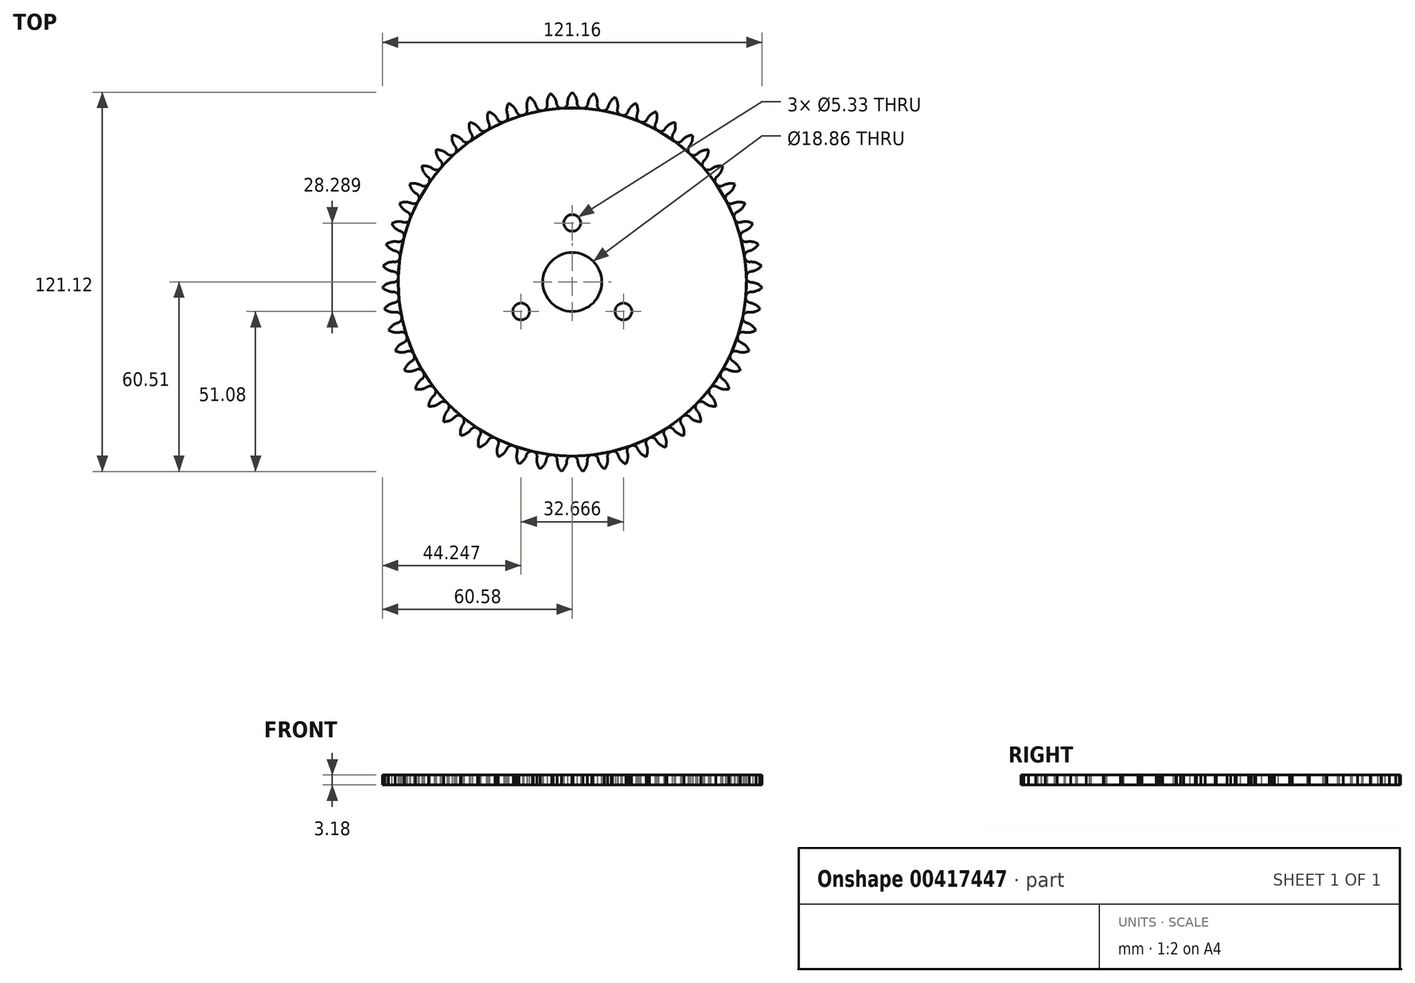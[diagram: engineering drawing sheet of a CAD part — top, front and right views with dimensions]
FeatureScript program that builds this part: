
annotation { "Feature Type Name" : "Feature", "Feature Type Description" : "" }
export const myFeature = defineFeature(function(context is Context, id is Id, definition is map)
    precondition{}
    {
        {
            assignVariable(context, id + "F0", {"name" : "Teeth", "anyValue" : 55});
        }
        {
            var Q0;
            Q0=qCreatedBy(makeId("Top.planeOp"),FACE);
            var sketch = newSketch(context, id + "F1", { "sketchPlane" : qUnion([Q0])});
            skCircle(sketch, "E0", {"center": v(0, 0) * mm, "radius": 55.58 * mm});
            skArc(sketch, "E1", {"start": v(-3.17, 55.5) * mm, "mid": v(-2, 55.98) * mm, "end": v(-1.52, 57.15) * mm});
            skLineSegment(sketch, "E2", {"start": v(-3.18, 57.15) * mm, "end": v(3.18, 57.15) * mm, "construction": true});
            skPoint(sketch, "E3", {"position": v(3.18, 55.5) * mm});
            skPoint(sketch, "E4", {"position": v(3.18, 58.8) * mm});
            skPoint(sketch, "E5", {"position": v(-3.17, 55.5) * mm});
            skPoint(sketch, "E6", {"position": v(-3.17, 58.8) * mm});
            skLineSegment(sketch, "E7", {"start": v(-3.17, 55.5) * mm, "end": v(3.18, 55.5) * mm});
            skLineSegment(sketch, "E8", {"start": v(0, 0) * mm, "end": v(0, 76.2) * mm, "construction": true});
            skLineSegment(sketch, "E9", {"start": v(0, 0) * mm, "end": v(-4.23, 76.2) * mm, "construction": true});
            skLineSegment(sketch, "E10", {"start": v(0, 0) * mm, "end": v(4.23, 76.2) * mm, "construction": true});
            skPoint(sketch, "E11", {"position": v(0, 60.6) * mm});
            skPoint(sketch, "E12", {"position": v(0, 53.68) * mm});
            skArc(sketch, "E13.trimOffspring", {"start": v(1.52, 57.15) * mm, "mid": v(1.13, 59.04) * mm, "end": v(0, 60.6) * mm});
            skArc(sketch, "E14.trimOffspring", {"start": v(1.52, 57.15) * mm, "mid": v(2, 55.98) * mm, "end": v(3.18, 55.5) * mm});
            skArc(sketch, "E15.trimOffspring", {"start": v(0, 60.6) * mm, "mid": v(-1.13, 59.04) * mm, "end": v(-1.52, 57.15) * mm});
            skCircle(sketch, "E16", {"center": v(0, 18.86) * mm, "radius": 2.67 * mm});
            skCircle(sketch, "E17", {"center": v(16.33, -9.43) * mm, "radius": 2.67 * mm});
            skCircle(sketch, "E18", {"center": v(-16.33, -9.43) * mm, "radius": 2.67 * mm});
            skLineSegment(sketch, "E19", {"start": v(-16.33, -9.43) * mm, "end": v(0, 18.86) * mm, "construction": true});
            skLineSegment(sketch, "E20", {"start": v(0, 18.86) * mm, "end": v(16.33, -9.43) * mm, "construction": true});
            skLineSegment(sketch, "E21", {"start": v(-16.33, -9.43) * mm, "end": v(16.33, -9.43) * mm, "construction": true});
            skLineSegment(sketch, "E22", {"start": v(-16.33, -9.43) * mm, "end": v(8.17, 4.71) * mm, "construction": true});
            skLineSegment(sketch, "E23", {"start": v(0, 18.86) * mm, "end": v(0, -9.43) * mm, "construction": true});
            skLineSegment(sketch, "E24", {"start": v(16.33, -9.43) * mm, "end": v(-8.17, 4.71) * mm, "construction": true});
            skCircle(sketch, "E25", {"center": v(0, 0) * mm, "radius": 9.43 * mm});
            skSolve(sketch);
        }
        {
            var Q0;
            Q0=qCreatedBy(makeId("Right.planeOp"),FACE);
            var sketch = newSketch(context, id + "F2", { "sketchPlane" : qUnion([Q0])});
            skLineSegment(sketch, "E26", {"start": v(0, 0) * mm, "end": v(0, 28.17) * mm, "construction": true});
            skSolve(sketch);
        }
        {
            var Q0;
            {var subQ0=sQuery(id+"F1.wireOp",EDGE,"E7");Q0=makeQuery(id+"F1.imprint","IMPRINT",FACE,{"disambiguationData":[TD([[makeQuery(id+"F1.imprint","IMPRINT",EDGE,{"derivedFrom":subQ0}),-1.0]])]});}
            extrude(context, id + "F3", {"entities" : qUnion([Q0]), "depth" : 3.17 * mm});
        }
        {
            var Q0;
            {var subQ1=sQuery(id+"F1.wireOp",EDGE,"E13.trimOffspring");Q0=makeQuery(id+"F1.imprint","IMPRINT",FACE,{"disambiguationData":[TD([[makeQuery(id+"F1.imprint","IMPRINT",EDGE,{"derivedFrom":subQ1}),1.0]])]});}
            extrude(context, id + "F4", {"entities" : qUnion([Q0]), "depth" : 3.17 * mm});
        }
        {
            var Q0;
            {var subQ5=sQuery(id+"F1.wireOp",EDGE,"E7");Q0=makeQuery(id+"F1.imprint","IMPRINT",FACE,{"disambiguationData":[TD([[makeQuery(id+"F1.imprint","IMPRINT",EDGE,{"derivedFrom":subQ5}),1.0]])]});}
            extrude(context, id + "F5", {"entities" : qUnion([Q0]), "depth" : 3.17 * mm});
        }
        {
            var Q0;
            Q0=makeQuery(id+"F5.opExtrude","SWEPT_BODY",BODY,{"disambiguationData":[OSD([sQuery(id+"F1.wireOp",EDGE,"E0"),sQuery(id+"F1.wireOp",EDGE,"E1"),sQuery(id+"F1.wireOp",EDGE,"E7"),sQuery(id+"F1.wireOp",EDGE,"E14.trimOffspring")])]});
            var Q1;
            Q1=makeQuery(id+"F4.opExtrude","SWEPT_BODY",BODY,{"disambiguationData":[OSD([sQuery(id+"F1.wireOp",EDGE,"E0"),sQuery(id+"F1.wireOp",EDGE,"E1"),sQuery(id+"F1.wireOp",EDGE,"E13.trimOffspring"),sQuery(id+"F1.wireOp",EDGE,"E14.trimOffspring"),sQuery(id+"F1.wireOp",EDGE,"E15.trimOffspring")])]});
            var Q2;
            Q2=sQuery(id+"F2.wireOp",EDGE,"E26");
            circularPattern(context, id + "F6", {"entities" : qUnion([Q0, Q1]), "axis" : qUnion([Q2]), "angle" : 360 * degree, "instanceCount" : getVariable(context, 'Teeth'), "equalSpace" : true});
        }
    });
